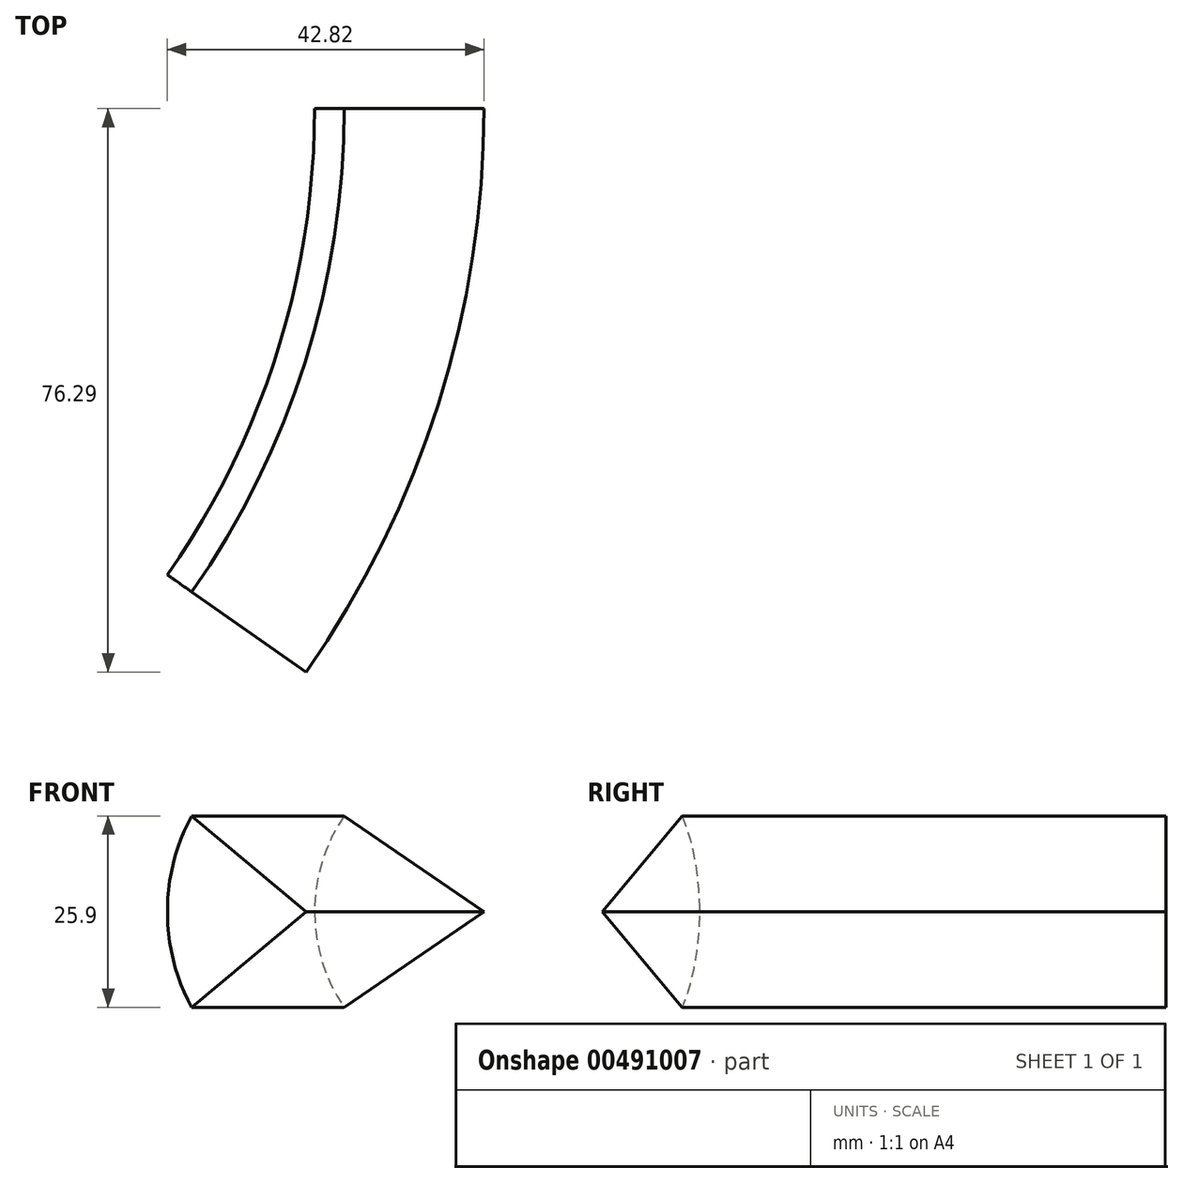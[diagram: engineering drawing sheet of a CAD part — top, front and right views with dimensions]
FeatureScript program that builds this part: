
annotation { "Feature Type Name" : "Feature", "Feature Type Description" : "" }
export const myFeature = defineFeature(function(context is Context, id is Id, definition is map)
    precondition{}
    {
        {
            var Q0;
            Q0=qCreatedBy(makeId("Front.planeOp"),FACE);
            var sketch = newSketch(context, id + "F0", { "sketchPlane" : qUnion([Q0])});
            skLineSegment(sketch, "E0", {"start": v(0, 0) * mm, "end": v(0, 41.44) * mm, "construction": true});
            skArc(sketch, "E1", {"start": v(114.1, 35.86) * mm, "mid": v(110.1, 22.91) * mm, "end": v(114.1, 9.96) * mm});
            skLineSegment(sketch, "E2", {"start": v(133, 22.91) * mm, "end": v(114.1, 35.86) * mm});
            skLineSegment(sketch, "E3", {"start": v(133, 22.91) * mm, "end": v(114.1, 9.96) * mm});
            skLineSegment(sketch, "E4", {"start": v(0, 0) * mm, "end": v(162.26, 0) * mm, "construction": true});
            skLineSegment(sketch, "E5", {"start": v(133, 22.91) * mm, "end": v(110.1, 22.91) * mm, "construction": true});
            skLineSegment(sketch, "E6", {"start": v(114.1, 9.96) * mm, "end": v(114.1, 22.91) * mm, "construction": true});
            skLineSegment(sketch, "E7", {"start": v(114.1, 22.91) * mm, "end": v(114.1, 35.86) * mm, "construction": true});
            skSolve(sketch);
        }
        {
            var Q0;
            Q0 = qSketchRegion(id + "F0", true);
            var Q1;
            Q1=sQuery(id+"F0.wireOp",EDGE,"E0");
            revolve(context, id + "F1", {"entities" : qUnion([Q0]), "axis" : qUnion([Q1]), "revolveType" : RevolveType.ONE_DIRECTION, "oppositeDirection" : true, "angle" : 35 * degree});
        }
    });
